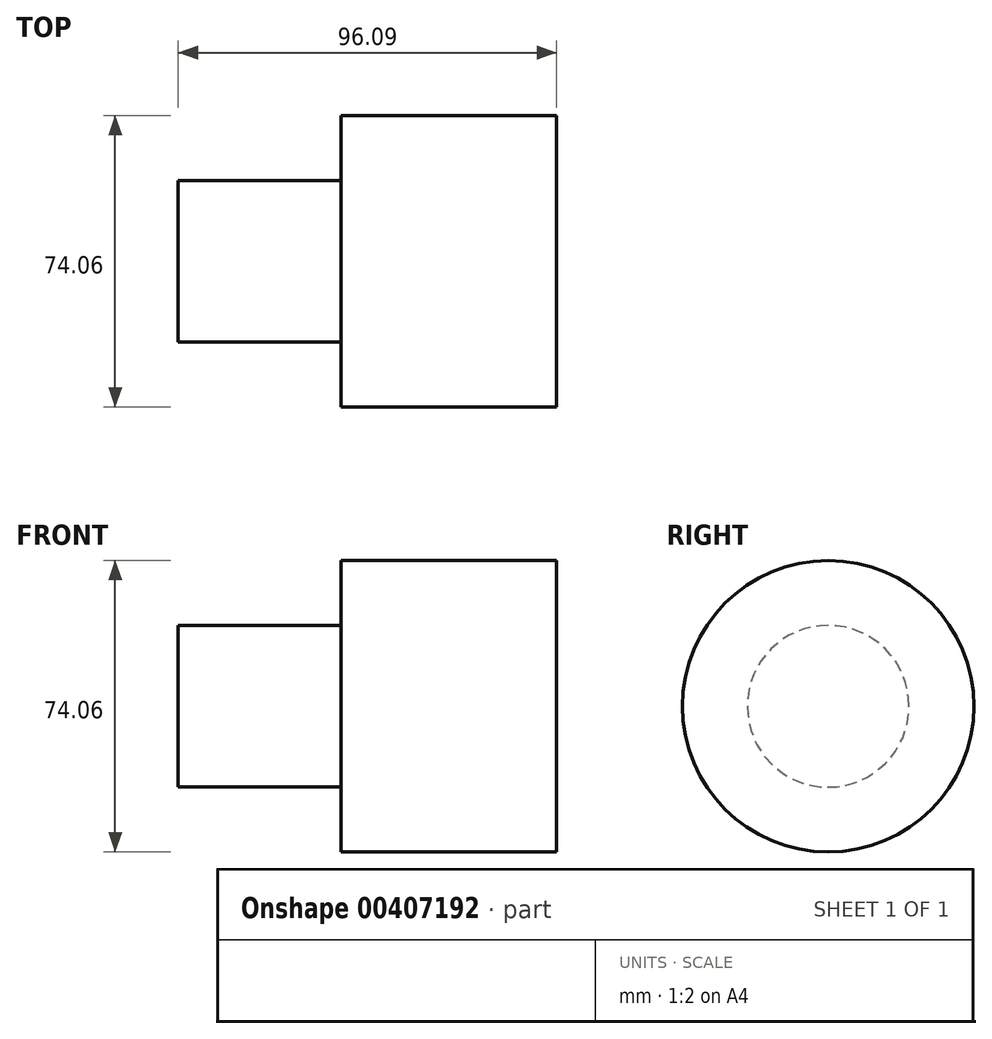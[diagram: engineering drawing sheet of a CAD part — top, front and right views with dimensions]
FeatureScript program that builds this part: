
annotation { "Feature Type Name" : "Feature", "Feature Type Description" : "" }
export const myFeature = defineFeature(function(context is Context, id is Id, definition is map)
    precondition{}
    {
        {
            var Q0;
            Q0=qCreatedBy(makeId("Front.planeOp"),FACE);
            var sketch = newSketch(context, id + "F0", { "sketchPlane" : qUnion([Q0])});
            skLineSegment(sketch, "E0", {"start": v(0, 0) * mm, "end": v(-96.1, 0) * mm});
            skLineSegment(sketch, "E1", {"start": v(-96.1, 0) * mm, "end": v(-96.1, 20.54) * mm});
            skLineSegment(sketch, "E2", {"start": v(-96.1, 20.54) * mm, "end": v(-54.74, 20.54) * mm});
            skLineSegment(sketch, "E3", {"start": v(-54.74, 20.54) * mm, "end": v(-54.74, 37.03) * mm});
            skLineSegment(sketch, "E4", {"start": v(-54.74, 37.03) * mm, "end": v(0, 37.03) * mm});
            skLineSegment(sketch, "E5", {"start": v(0, 37.03) * mm, "end": v(0, 0) * mm});
            skLineSegment(sketch, "E6", {"start": v(0, 0) * mm, "end": v(37.76, 0) * mm, "construction": true});
            skSolve(sketch);
        }
        {
            var Q0;
            Q0=makeQuery(id+"F0.imprint","IMPRINT",FACE,{"disambiguationData":[TD([[makeQuery(id+"F0.imprint","IMPRINT",EDGE,{"derivedFrom":sQuery(id+"F0.wireOp",EDGE,"E0")}),-1.0]])]});
            var Q1;
            Q1=sQuery(id+"F0.wireOp",EDGE,"E6");
            revolve(context, id + "F1", {"entities" : qUnion([Q0]), "axis" : qUnion([Q1]), "revolveType" : RevolveType.FULL});
        }
    });
